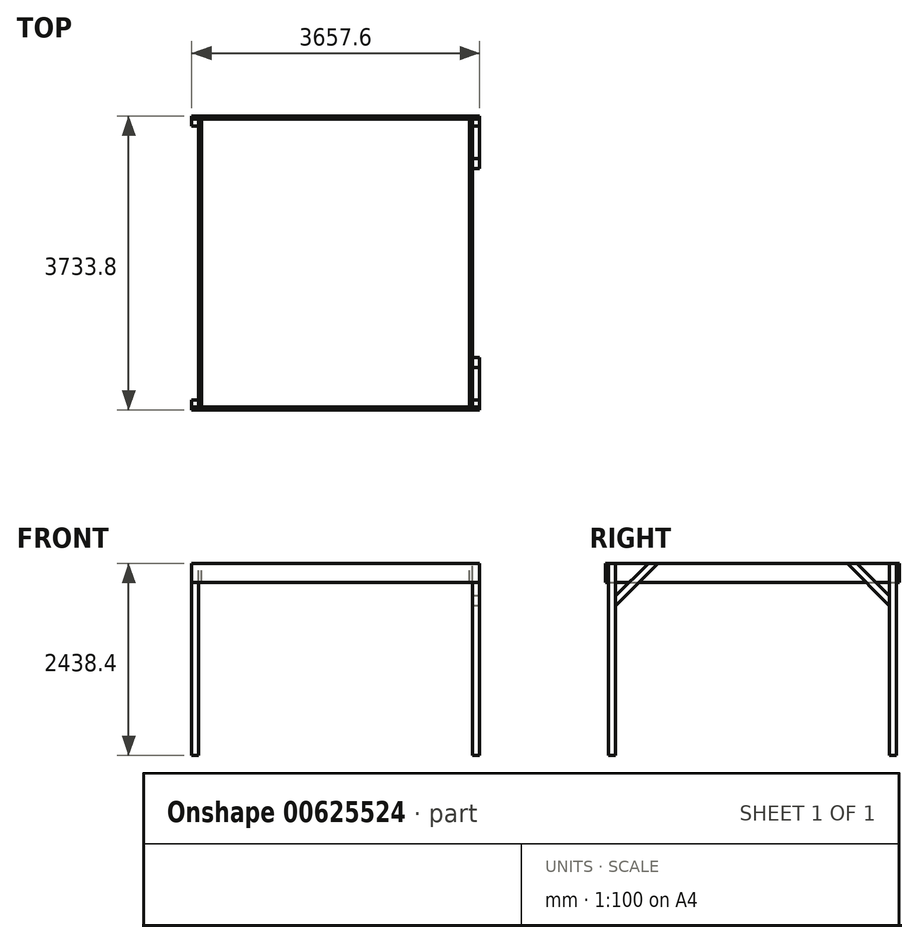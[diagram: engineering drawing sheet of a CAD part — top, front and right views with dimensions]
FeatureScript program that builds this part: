
annotation { "Feature Type Name" : "Feature", "Feature Type Description" : "" }
export const myFeature = defineFeature(function(context is Context, id is Id, definition is map)
    precondition{}
    {
        {
            var Q0;
            Q0=qCreatedBy(makeId("Top.planeOp"),FACE);
            var sketch = newSketch(context, id + "F0", { "sketchPlane" : qUnion([Q0])});
            skLineSegment(sketch, "E0.bottom", {"start": v(-1828.8, -1828.8) * mm, "end": v(1828.8, -1828.8) * mm, "construction": true});
            skLineSegment(sketch, "E0.top", {"start": v(-1828.8, 1828.8) * mm, "end": v(1828.8, 1828.8) * mm, "construction": true});
            skLineSegment(sketch, "E0.left", {"start": v(-1828.8, -1828.8) * mm, "end": v(-1828.8, 1828.8) * mm, "construction": true});
            skLineSegment(sketch, "E0.right", {"start": v(1828.8, -1828.8) * mm, "end": v(1828.8, 1828.8) * mm, "construction": true});
            skLineSegment(sketch, "E1", {"start": v(-1828.8, 0) * mm, "end": v(1828.8, 0) * mm, "construction": true});
            skLineSegment(sketch, "E2", {"start": v(0, 1828.8) * mm, "end": v(0, -1828.8) * mm, "construction": true});
            skLineSegment(sketch, "E3.bottom", {"start": v(-1828.8, 1828.8) * mm, "end": v(-1739.9, 1828.8) * mm});
            skLineSegment(sketch, "E3.top", {"start": v(-1828.8, 1739.9) * mm, "end": v(-1739.9, 1739.9) * mm});
            skLineSegment(sketch, "E3.left", {"start": v(-1828.8, 1828.8) * mm, "end": v(-1828.8, 1739.9) * mm});
            skLineSegment(sketch, "E3.right", {"start": v(-1739.9, 1828.8) * mm, "end": v(-1739.9, 1739.9) * mm});
            skLineSegment(sketch, "E4.bottom", {"start": v(1828.8, 1828.8) * mm, "end": v(1739.9, 1828.8) * mm});
            skLineSegment(sketch, "E4.top", {"start": v(1828.8, 1739.9) * mm, "end": v(1739.9, 1739.9) * mm});
            skLineSegment(sketch, "E4.left", {"start": v(1828.8, 1828.8) * mm, "end": v(1828.8, 1739.9) * mm});
            skLineSegment(sketch, "E4.right", {"start": v(1739.9, 1828.8) * mm, "end": v(1739.9, 1739.9) * mm});
            skLineSegment(sketch, "E5.bottom", {"start": v(1828.8, -1828.8) * mm, "end": v(1739.9, -1828.8) * mm});
            skLineSegment(sketch, "E5.top", {"start": v(1828.8, -1739.9) * mm, "end": v(1739.9, -1739.9) * mm});
            skLineSegment(sketch, "E5.left", {"start": v(1828.8, -1828.8) * mm, "end": v(1828.8, -1739.9) * mm});
            skLineSegment(sketch, "E5.right", {"start": v(1739.9, -1828.8) * mm, "end": v(1739.9, -1739.9) * mm});
            skLineSegment(sketch, "E6.bottom", {"start": v(-1828.8, -1828.8) * mm, "end": v(-1739.9, -1828.8) * mm});
            skLineSegment(sketch, "E6.top", {"start": v(-1828.8, -1739.9) * mm, "end": v(-1739.9, -1739.9) * mm});
            skLineSegment(sketch, "E6.left", {"start": v(-1828.8, -1828.8) * mm, "end": v(-1828.8, -1739.9) * mm});
            skLineSegment(sketch, "E6.right", {"start": v(-1739.9, -1828.8) * mm, "end": v(-1739.9, -1739.9) * mm});
            skSolve(sketch);
        }
        {
            var Q0;
            Q0 = qSketchRegion(id + "F0", true);
            extrude(context, id + "F1", {"entities" : qUnion([Q0]), "depth" : 2438.4 * mm, "offsetDistance" : 25.4 * mm});
        }
        {
            var Q0;
            Q0=makeQuery(id+"F1.opExtrude","CAP_FACE",FACE,{"disambiguationData":[OSD([sQuery(id+"F0.wireOp",EDGE,"E6.bottom"),sQuery(id+"F0.wireOp",EDGE,"E6.top"),sQuery(id+"F0.wireOp",EDGE,"E6.left"),sQuery(id+"F0.wireOp",EDGE,"E6.right")])],"isStart":false});
            var sketch = newSketch(context, id + "F2", { "sketchPlane" : qUnion([Q0])});
            skLineSegment(sketch, "E7", {"start": v(-1701.8, -1828.8) * mm, "end": v(-1701.8, 1828.8) * mm});
            skLineSegment(sketch, "E8", {"start": v(-1701.8, -1828.8) * mm, "end": v(-1739.9, -1828.8) * mm});
            skLineSegment(sketch, "E9", {"start": v(-1701.8, 1828.8) * mm, "end": v(-1739.9, 1828.8) * mm});
            skLineSegment(sketch, "E10", {"start": v(-1739.9, 1828.8) * mm, "end": v(-1739.9, -1828.8) * mm});
            skLineSegment(sketch, "E11.bottom", {"start": v(1739.9, -1828.8) * mm, "end": v(1701.8, -1828.8) * mm});
            skLineSegment(sketch, "E11.top", {"start": v(1739.9, 1828.8) * mm, "end": v(1701.8, 1828.8) * mm});
            skLineSegment(sketch, "E11.left", {"start": v(1739.9, -1828.8) * mm, "end": v(1739.9, 1828.8) * mm});
            skLineSegment(sketch, "E11.right", {"start": v(1701.8, -1828.8) * mm, "end": v(1701.8, 1828.8) * mm});
            skSolve(sketch);
        }
        {
            var Q0;
            Q0 = qSketchRegion(id + "F2", true);
            extrude(context, id + "F3", {"entities" : qUnion([Q0]), "oppositeDirection" : true, "depth" : 241.3 * mm, "offsetDistance" : 25.4 * mm});
        }
        {
            var Q0;
            Q0=makeQuery(id+"F1.opExtrude","CAP_FACE",FACE,{"disambiguationData":[OSD([sQuery(id+"F0.wireOp",EDGE,"E6.bottom"),sQuery(id+"F0.wireOp",EDGE,"E6.top"),sQuery(id+"F0.wireOp",EDGE,"E6.left"),sQuery(id+"F0.wireOp",EDGE,"E6.right")])],"isStart":false});
            var sketch = newSketch(context, id + "F4", { "sketchPlane" : qUnion([Q0])});
            skLineSegment(sketch, "E12.bottom", {"start": v(-1828.8, -1828.8) * mm, "end": v(1828.8, -1828.8) * mm});
            skLineSegment(sketch, "E12.top", {"start": v(-1828.8, -1866.9) * mm, "end": v(1828.8, -1866.9) * mm});
            skLineSegment(sketch, "E12.left", {"start": v(-1828.8, -1828.8) * mm, "end": v(-1828.8, -1866.9) * mm});
            skLineSegment(sketch, "E12.right", {"start": v(1828.8, -1828.8) * mm, "end": v(1828.8, -1866.9) * mm});
            skLineSegment(sketch, "E13.bottom", {"start": v(-1828.8, 1866.9) * mm, "end": v(1828.8, 1866.9) * mm});
            skLineSegment(sketch, "E13.top", {"start": v(-1828.8, 1828.8) * mm, "end": v(1828.8, 1828.8) * mm});
            skLineSegment(sketch, "E13.left", {"start": v(-1828.8, 1866.9) * mm, "end": v(-1828.8, 1828.8) * mm});
            skLineSegment(sketch, "E13.right", {"start": v(1828.8, 1866.9) * mm, "end": v(1828.8, 1828.8) * mm});
            skSolve(sketch);
        }
        {
            var Q0;
            Q0 = qSketchRegion(id + "F4", true);
            var Q1;
            Q1=makeQuery(id+"F3.opExtrude","CAP_VERTEX",VERTEX,{"disambiguationData":[OSD([sQuery(id+"F2.wireOp",EDGE,"E11.bottom"),sQuery(id+"F2.wireOp",EDGE,"E11.right")])],"isStart":false});
            extrude(context, id + "F5", {"entities" : qUnion([Q0]), "endBound" : BoundingType.UP_TO_VERTEX, "oppositeDirection" : true, "depth" : 25.4 * mm, "endBoundEntityVertex" : qUnion([Q1]), "offsetDistance" : 25.4 * mm});
        }
        {
            var Q0;
            Q0=makeQuery(id+"F3.opExtrude","SWEPT_FACE",FACE,{"disambiguationData":[OSD([sQuery(id+"F2.wireOp",EDGE,"E11.left")])]});
            var sketch = newSketch(context, id + "F6", { "sketchPlane" : qUnion([Q0])});
            skLineSegment(sketch, "E14", {"start": v(-1739.9, 2025.3) * mm, "end": v(-1326.8, 2438.4) * mm});
            skLineSegment(sketch, "E15", {"start": v(-1326.8, 2438.4) * mm, "end": v(-1201.08, 2438.4) * mm});
            skLineSegment(sketch, "E16", {"start": v(-1201.08, 2438.4) * mm, "end": v(-1201.08, 2438.4) * mm});
            skLineSegment(sketch, "E17", {"start": v(-1739.9, 1899.58) * mm, "end": v(-1739.9, 2025.3) * mm});
            skLineSegment(sketch, "E18", {"start": v(-1739.9, 1899.58) * mm, "end": v(-1201.08, 2438.4) * mm});
            skLineSegment(sketch, "E19", {"start": v(-1739.9, 2438.4) * mm, "end": v(-1326.8, 2438.4) * mm, "construction": true});
            skLineSegment(sketch, "E20", {"start": v(-1739.9, 2025.3) * mm, "end": v(-1739.9, 2438.4) * mm, "construction": true});
            skLineSegment(sketch, "E21", {"start": v(1739.9, 2438.4) * mm, "end": v(1326.8, 2438.4) * mm, "construction": true});
            skLineSegment(sketch, "E22", {"start": v(1326.8, 2438.4) * mm, "end": v(1739.9, 2438.4) * mm, "construction": true});
            skLineSegment(sketch, "E23", {"start": v(1739.9, 2438.4) * mm, "end": v(1739.9, 2025.3) * mm, "construction": true});
            skLineSegment(sketch, "E24", {"start": v(1739.9, 2025.3) * mm, "end": v(1739.9, 1899.58) * mm});
            skLineSegment(sketch, "E25", {"start": v(1739.9, 1899.58) * mm, "end": v(1201.08, 2438.4) * mm});
            skLineSegment(sketch, "E26", {"start": v(1201.08, 2438.4) * mm, "end": v(1326.8, 2438.4) * mm});
            skLineSegment(sketch, "E27", {"start": v(1326.8, 2438.4) * mm, "end": v(1739.9, 2025.3) * mm});
            skSolve(sketch);
        }
        {
            var Q0;
            Q0 = qSketchRegion(id + "F6", true);
            var Q1;
            Q1=makeQuery(id+"F1.opExtrude","CAP_VERTEX",VERTEX,{"disambiguationData":[OSD([sQuery(id+"F0.wireOp",EDGE,"E4.top"),sQuery(id+"F0.wireOp",EDGE,"E4.left")])],"isStart":false});
            extrude(context, id + "F7", {"entities" : qUnion([Q0]), "endBound" : BoundingType.UP_TO_VERTEX, "depth" : 25.4 * mm, "endBoundEntityVertex" : qUnion([Q1]), "offsetDistance" : 25.4 * mm});
        }
    });
